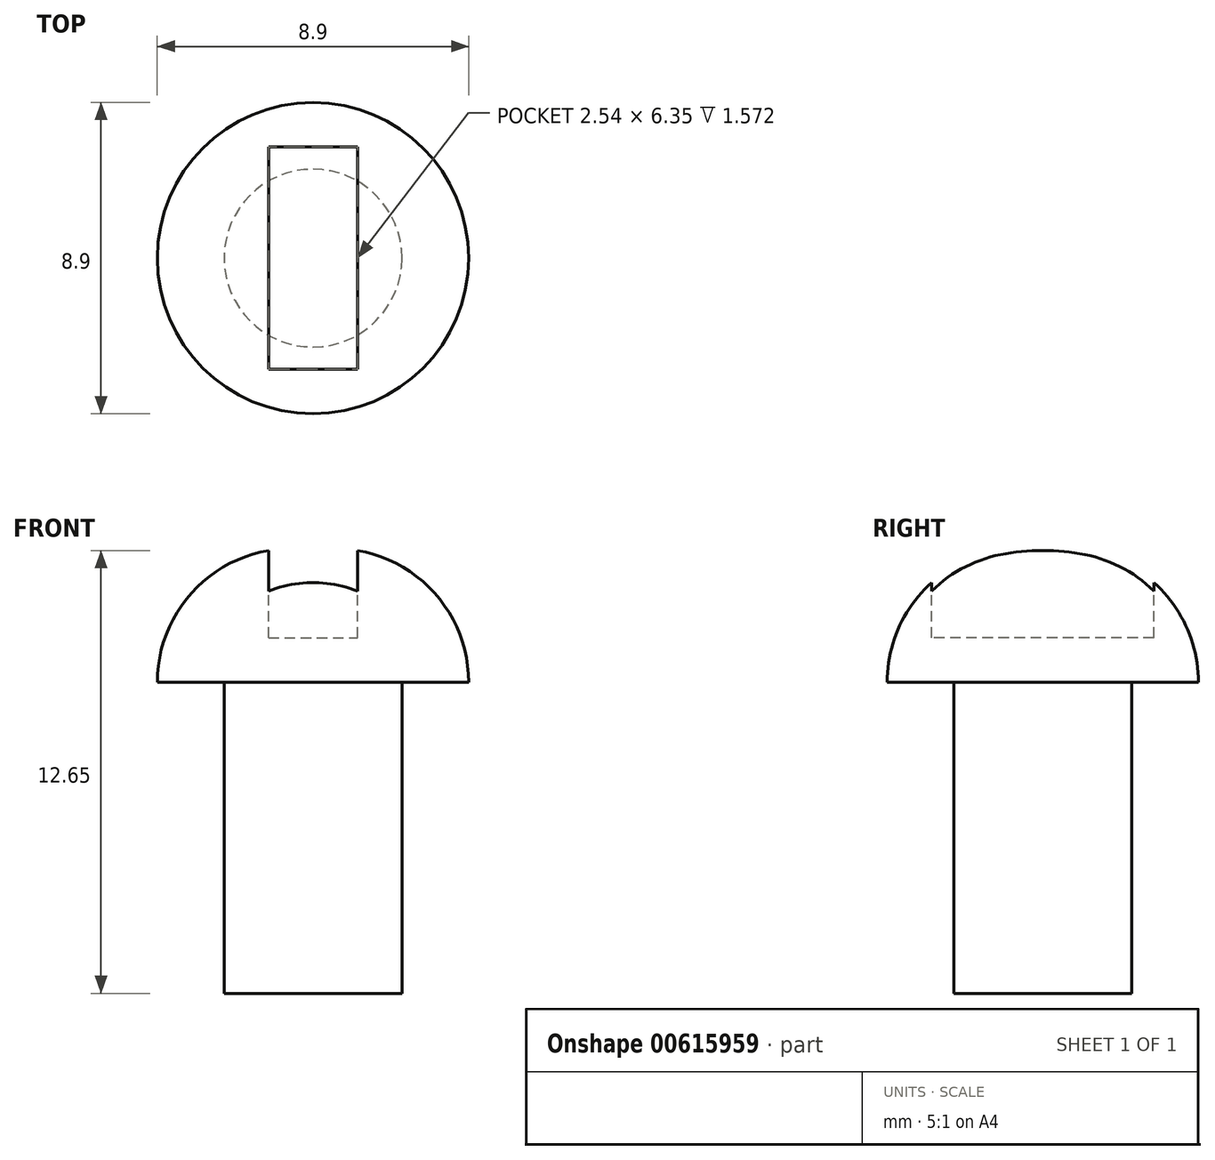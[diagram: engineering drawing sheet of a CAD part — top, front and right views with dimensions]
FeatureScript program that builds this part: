
annotation { "Feature Type Name" : "Feature", "Feature Type Description" : "" }
export const myFeature = defineFeature(function(context is Context, id is Id, definition is map)
    precondition{}
    {
        {
            var Q0;
            Q0=qCreatedBy(makeId("Top.planeOp"),FACE);
            var sketch = newSketch(context, id + "F0", { "sketchPlane" : qUnion([Q0])});
            skCircle(sketch, "E0", {"center": v(0, 0) * mm, "radius": 2.54 * mm});
            skSolve(sketch);
        }
        {
            var Q0;
            Q0 = qSketchRegion(id + "F0", true);
            extrude(context, id + "F1", {"entities" : qUnion([Q0]), "depth" : 8.9 * mm, "offsetDistance" : 25.4 * mm});
        }
        {
            var Q0;
            Q0=makeQuery(id+"F1.opExtrude","CAP_FACE",FACE,{"disambiguationData":[OSD([sQuery(id+"F0.wireOp",EDGE,"E0")])],"isStart":false});
            var sketch = newSketch(context, id + "F2", { "sketchPlane" : qUnion([Q0])});
            skCircle(sketch, "E1", {"center": v(0, 0) * mm, "radius": 4.45 * mm});
            skSolve(sketch);
        }
        {
            var Q0;
            Q0 = qSketchRegion(id + "F2", true);
            extrude(context, id + "F3", {"entities" : qUnion([Q0]), "operationType" : NewBodyOperationType.ADD, "depth" : 3.8 * mm, "offsetDistance" : 25.4 * mm});
        }
        {
            var Q0;
            Q0=makeQuery(id+"F3.opExtrude","CAP_FACE",FACE,{"disambiguationData":[OSD([sQuery(id+"F2.wireOp",EDGE,"E1")])],"isStart":false});
            var sketch = newSketch(context, id + "F4", { "sketchPlane" : qUnion([Q0])});
            skLineSegment(sketch, "E2.bottom", {"start": v(-1.27, 3.18) * mm, "end": v(1.27, 3.18) * mm});
            skLineSegment(sketch, "E2.top", {"start": v(-1.27, -3.18) * mm, "end": v(1.27, -3.18) * mm});
            skLineSegment(sketch, "E2.left", {"start": v(-1.27, 3.18) * mm, "end": v(-1.27, -3.17) * mm});
            skLineSegment(sketch, "E2.right", {"start": v(1.27, 3.18) * mm, "end": v(1.27, -3.17) * mm});
            skSolve(sketch);
        }
        {
            var Q0;
            Q0 = qSketchRegion(id + "F4", true);
            extrude(context, id + "F5", {"entities" : qUnion([Q0]), "operationType" : NewBodyOperationType.REMOVE, "oppositeDirection" : true, "depth" : 2.54 * mm, "offsetDistance" : 25.4 * mm});
        }
        {
            var Q0;
            Q0=makeQuery(id+"F3.opExtrude","CAP_EDGE",EDGE,{"disambiguationData":[OSD([sQuery(id+"F2.wireOp",EDGE,"E1")])],"isStart":false});
            fillet(context, id + "F6", {"entities" : qUnion([Q0]), "radius" : 3.8 * mm, "tangentPropagation" : true, "allowEdgeOverflow" : false});
        }
    });
